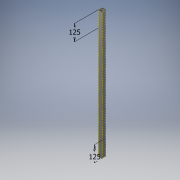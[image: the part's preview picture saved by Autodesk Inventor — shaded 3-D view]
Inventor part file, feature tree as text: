
AUTODESK INVENTOR PART (.ipt)
format: ipt  version: 2019 (Build 230136000, 136)  size: 117,248 bytes
history: native  units: mm
features: sketch x3, projected_geometry x2, extrude x1
ambient origin geometry x8: Origin, YZ Plane, XZ Plane, XY Plane, X Axis, Y Axis, Z Axis, Center Point
bodies: Solid1 (feature_tree)
feature tree (6):
  extrude  "Extrusion1"  Depth=30.0mm
  sketch  "Sketch2"  dims[d2=2.5mm]
  sketch  "Sketch3"  dims[d3=2.5mm d4=1000.0mm d5=0.0mm d6=125.0mm d7=125.0mm]
  sketch  "Sketch1"  dims[d0=30.0mm d1=30.0mm]
  projected_geometry  "Projected Loop1"
  projected_geometry  "Projected Loop2"
